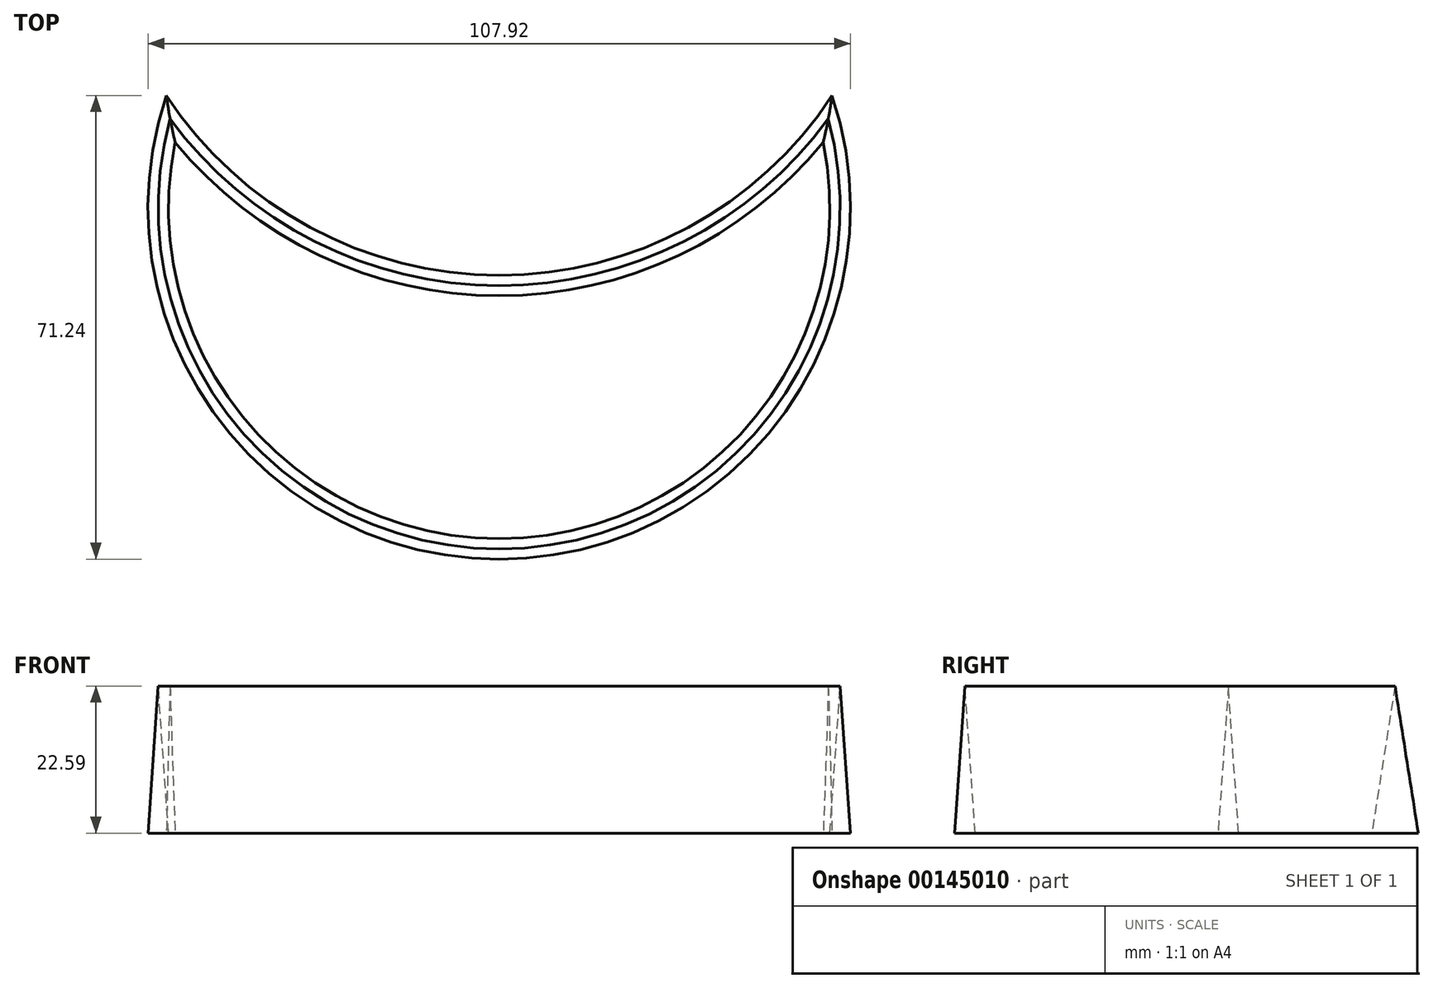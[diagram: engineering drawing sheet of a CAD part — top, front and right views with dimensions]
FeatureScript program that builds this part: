
annotation { "Feature Type Name" : "Feature", "Feature Type Description" : "" }
export const myFeature = defineFeature(function(context is Context, id is Id, definition is map)
    precondition{}
    {
        {
            var Q0;
            Q0=qCreatedBy(makeId("Top.planeOp"),FACE);
            var sketch = newSketch(context, id + "F0", { "sketchPlane" : qUnion([Q0])});
            skArc(sketch, "E0", {"start": v(-49.78, 10.12) * mm, "mid": v(0, -50.8) * mm, "end": v(49.78, 10.12) * mm});
            skLineSegment(sketch, "E1", {"start": v(0, 0) * mm, "end": v(0, 74.06) * mm, "construction": true});
            skArc(sketch, "E2", {"start": v(-49.78, 10.12) * mm, "mid": v(0, -13.49) * mm, "end": v(49.78, 10.12) * mm});
            skArc(sketch, "E3.0", {"start": v(-51.12, 17.28) * mm, "mid": v(0, -10.33) * mm, "end": v(51.12, 17.28) * mm});
            skArc(sketch, "E3.1", {"start": v(-51.12, 17.28) * mm, "mid": v(0, -53.96) * mm, "end": v(51.12, 17.28) * mm});
            skSolve(sketch);
        }
        {
            var Q0;
            Q0=makeQuery(id+"F0.imprint","IMPRINT",FACE,{"disambiguationData":[TD([[makeQuery(id+"F0.imprint","IMPRINT",EDGE,{"derivedFrom":sQuery(id+"F0.wireOp",EDGE,"E0")}),-1.0]])]});
            extrude(context, id + "F1", {"entities" : qUnion([Q0]), "depth" : 25.4 * mm, "hasDraft" : true, "draftAngle" : 4 * degree, "draftPullDirection" : true});
        }
    });
